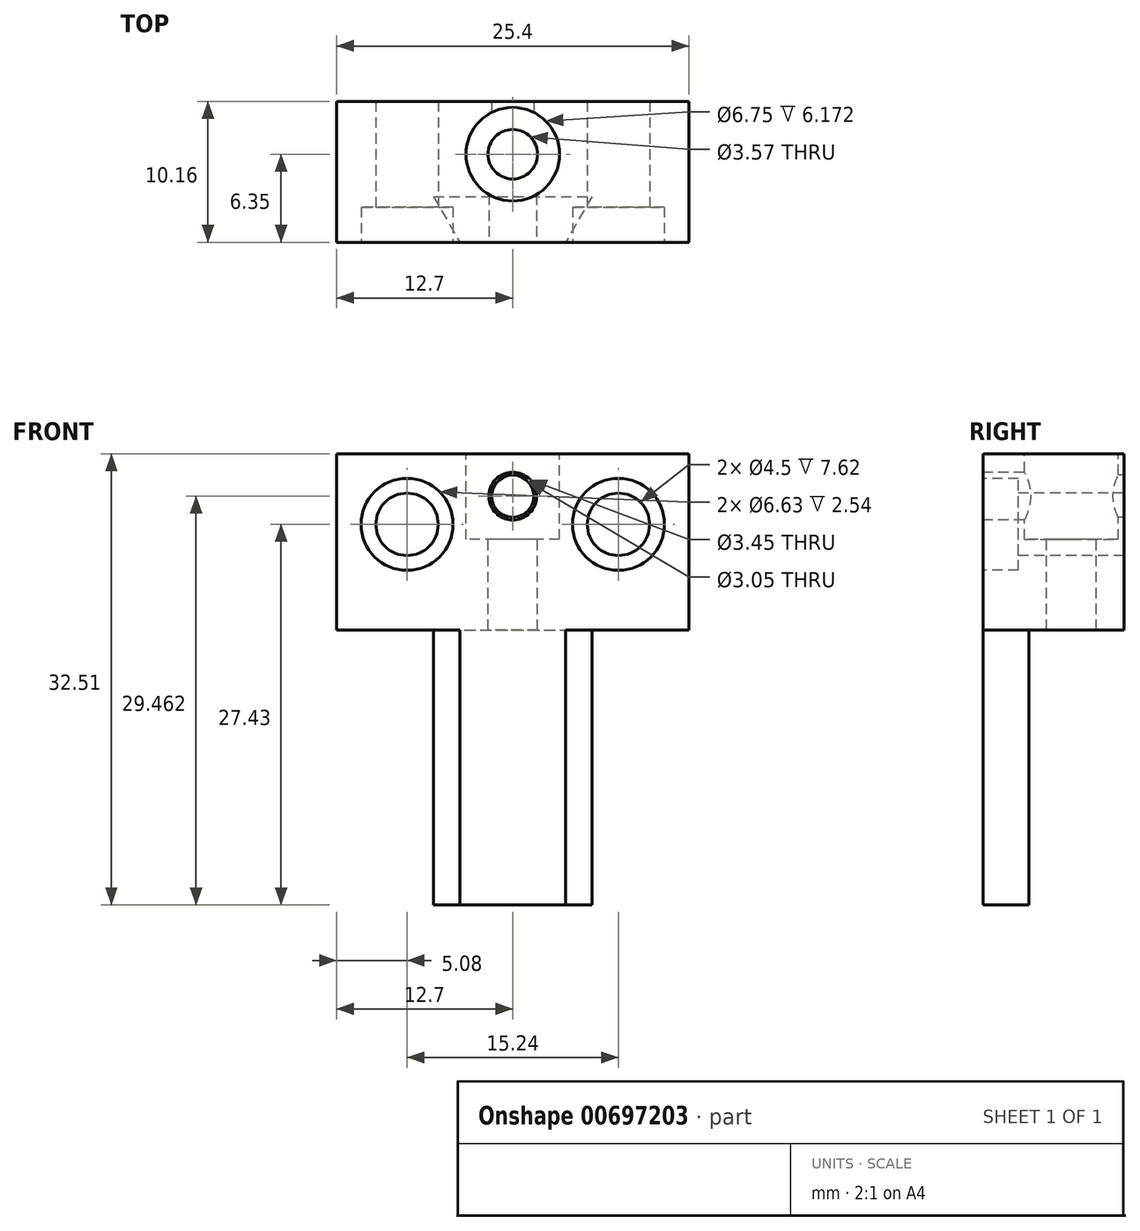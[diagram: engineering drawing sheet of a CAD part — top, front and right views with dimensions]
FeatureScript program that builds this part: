
annotation { "Feature Type Name" : "Feature", "Feature Type Description" : "" }
export const myFeature = defineFeature(function(context is Context, id is Id, definition is map)
    precondition{}
    {
        {
            var Q0;
            Q0=qCreatedBy(makeId("Top.planeOp"),FACE);
            var sketch = newSketch(context, id + "F0", { "sketchPlane" : qUnion([Q0])});
            skLineSegment(sketch, "E0.bottom", {"start": v(0, 0) * mm, "end": v(25.4, 0) * mm});
            skLineSegment(sketch, "E0.top", {"start": v(0, 10.16) * mm, "end": v(25.4, 10.16) * mm});
            skLineSegment(sketch, "E0.left", {"start": v(0, 0) * mm, "end": v(0, 10.16) * mm});
            skLineSegment(sketch, "E0.right", {"start": v(25.4, 0) * mm, "end": v(25.4, 10.16) * mm});
            skSolve(sketch);
        }
        {
            var Q0;
            Q0=makeQuery(id+"F0.imprint","IMPRINT",FACE,{"disambiguationData":[TD([[makeQuery(id+"F0.imprint","IMPRINT",EDGE,{"derivedFrom":sQuery(id+"F0.wireOp",EDGE,"E0.bottom")}),1.0]])]});
            extrude(context, id + "F1", {"entities" : qUnion([Q0]), "depth" : 12.7 * mm, "offsetDistance" : 25.4 * mm});
        }
        {
            var Q0;
            Q0=makeQuery(id+"F1.opExtrude","CAP_FACE",FACE,{"disambiguationData":[OSD([sQuery(id+"F0.wireOp",EDGE,"E0.bottom"),sQuery(id+"F0.wireOp",EDGE,"E0.top"),sQuery(id+"F0.wireOp",EDGE,"E0.left"),sQuery(id+"F0.wireOp",EDGE,"E0.right")])],"isStart":true});
            var sketch = newSketch(context, id + "F2", { "sketchPlane" : qUnion([Q0])});
            skLineSegment(sketch, "E1", {"start": v(0, -3.3) * mm, "end": v(6.99, -3.3) * mm});
            skLineSegment(sketch, "E2", {"start": v(6.99, -3.3) * mm, "end": v(8.9, 0) * mm});
            skLineSegment(sketch, "E3", {"start": v(6.99, -3.3) * mm, "end": v(18.41, -3.3) * mm});
            skLineSegment(sketch, "E4", {"start": v(18.41, -3.3) * mm, "end": v(16.5, 0) * mm});
            skLineSegment(sketch, "E5", {"start": v(8.9, 0) * mm, "end": v(16.5, 0) * mm});
            skSolve(sketch);
        }
        {
            var Q0;
            Q0=makeQuery(id+"F2.imprint","IMPRINT",FACE,{"disambiguationData":[TD([[makeQuery(id+"F2.imprint","IMPRINT",EDGE,{"derivedFrom":sQuery(id+"F2.wireOp",EDGE,"E2")}),-1.0]])]});
            extrude(context, id + "F3", {"entities" : qUnion([Q0]), "operationType" : NewBodyOperationType.ADD, "depth" : 19.8 * mm, "offsetDistance" : 25.4 * mm});
        }
        {
            var Q0;
            Q0=makeQuery(id+"F3.boolean.opBoolean","MERGE",FACE,{"derivedFrom":[makeQuery(id+"F1.opExtrude","SWEPT_FACE",FACE,{"disambiguationData":[OSD([sQuery(id+"F0.wireOp",EDGE,"E0.bottom")])]}),makeQuery(id+"F3.opExtrude","SWEPT_FACE",FACE,{"disambiguationData":[OSD([sQuery(id+"F2.wireOp",EDGE,"E5")])]})]});
            var sketch = newSketch(context, id + "F4", { "sketchPlane" : qUnion([Q0])});
            skLineSegment(sketch, "E6", {"start": v(0, 7.62) * mm, "end": v(5.08, 7.62) * mm});
            skLineSegment(sketch, "E7", {"start": v(5.08, 7.62) * mm, "end": v(5.08, 12.7) * mm});
            skLineSegment(sketch, "E8", {"start": v(5.08, 7.62) * mm, "end": v(20.32, 7.62) * mm});
            skLineSegment(sketch, "E9", {"start": v(20.32, 7.62) * mm, "end": v(20.32, 12.7) * mm});
            skLineSegment(sketch, "E10", {"start": v(20.32, 7.62) * mm, "end": v(25.4, 7.62) * mm});
            skLineSegment(sketch, "E11", {"start": v(12.7, 12.7) * mm, "end": v(12.7, 9.65) * mm});
            skLineSegment(sketch, "E12", {"start": v(12.7, 9.65) * mm, "end": v(0, 9.65) * mm});
            skSolve(sketch);
        }
        {
            var Q0;
            Q0=sQuery(id+"F4.wireOp",VERTEX,"E8.start");
            var Q1;
            Q1=sQuery(id+"F4.wireOp",VERTEX,"E10.start");
            var Q2;
            Q2=makeQuery(id+"F1.opExtrude","SWEPT_BODY",BODY,{"disambiguationData":[OSD([sQuery(id+"F0.wireOp",EDGE,"E0.bottom"),sQuery(id+"F0.wireOp",EDGE,"E0.top"),sQuery(id+"F0.wireOp",EDGE,"E0.left"),sQuery(id+"F0.wireOp",EDGE,"E0.right")])]});
            hole(context, id + "F5", {"style" : HoleStyle.C_BORE, "endStyle" : HoleEndStyle.THROUGH, "holeDiameter" : 4.5 * mm, "cBoreDiameter" : 6.63 * mm, "cBoreDepth" : 2.54 * mm, "majorDiameter" : 6.35 * mm, "isTappedThrough" : true, "tappedDepth" : 12.7 * mm, "tapClearance" : 3, "locations" : qUnion([Q0, Q1]), "scope" : qUnion([Q2])});
        }
        {
            var Q0;
            Q0=makeQuery(id+"F1.opExtrude","CAP_FACE",FACE,{"disambiguationData":[OSD([sQuery(id+"F0.wireOp",EDGE,"E0.bottom"),sQuery(id+"F0.wireOp",EDGE,"E0.top"),sQuery(id+"F0.wireOp",EDGE,"E0.left"),sQuery(id+"F0.wireOp",EDGE,"E0.right")])],"isStart":false});
            var sketch = newSketch(context, id + "F6", { "sketchPlane" : qUnion([Q0])});
            skLineSegment(sketch, "E13", {"start": v(12.7, 10.16) * mm, "end": v(12.7, 6.35) * mm});
            skLineSegment(sketch, "E14", {"start": v(12.7, 6.35) * mm, "end": v(25.4, 6.35) * mm});
            skSolve(sketch);
        }
        {
            var Q0;
            Q0=sQuery(id+"F6.wireOp",VERTEX,"E13.end");
            var Q1;
            Q1=makeQuery(id+"F1.opExtrude","SWEPT_BODY",BODY,{"disambiguationData":[OSD([sQuery(id+"F0.wireOp",EDGE,"E0.bottom"),sQuery(id+"F0.wireOp",EDGE,"E0.top"),sQuery(id+"F0.wireOp",EDGE,"E0.left"),sQuery(id+"F0.wireOp",EDGE,"E0.right")])]});
            hole(context, id + "F7", {"style" : HoleStyle.C_BORE, "endStyle" : HoleEndStyle.THROUGH, "holeDiameter" : 3.57 * mm, "cBoreDiameter" : 6.75 * mm, "cBoreDepth" : 6.17 * mm, "majorDiameter" : 6.35 * mm, "isTappedThrough" : true, "tappedDepth" : 12.7 * mm, "tapClearance" : 3, "locations" : qUnion([Q0]), "scope" : qUnion([Q1])});
        }
        {
            var Q0;
            Q0=sQuery(id+"F4.wireOp",VERTEX,"E12.start");
            var Q1;
            Q1=makeQuery(id+"F1.opExtrude","SWEPT_BODY",BODY,{"disambiguationData":[OSD([sQuery(id+"F0.wireOp",EDGE,"E0.bottom"),sQuery(id+"F0.wireOp",EDGE,"E0.top"),sQuery(id+"F0.wireOp",EDGE,"E0.left"),sQuery(id+"F0.wireOp",EDGE,"E0.right")])]});
            hole(context, id + "F8", {"style" : HoleStyle.SIMPLE, "endStyle" : HoleEndStyle.BLIND, "standardTappedOrClearance" : lookupTablePath({ "standard" : "ANSI", "engagement" : "75%", "pitch" : "32 tpi", "size" : "#8", "type" : "Tapped" }), "standardBlindInLast" : lookupTablePath({ "standard" : "ANSI", "engagement" : "75%", "pitch" : "32 tpi", "size" : "#8", "type" : "Tapped" }), "holeDiameter" : 3.45 * mm, "majorDiameter" : 4.17 * mm, "showTappedDepth" : true, "holeDepth" : 6.35 * mm, "isTappedThrough" : true, "tappedDepth" : 3.97 * mm, "tapClearance" : 3, "locations" : qUnion([Q0]), "scope" : qUnion([Q1])});
        }
        {
            var Q0;
            Q0=sQuery(id+"F4.wireOp",VERTEX,"E12.start");
            var Q1;
            Q1=makeQuery(id+"F1.opExtrude","SWEPT_BODY",BODY,{"disambiguationData":[OSD([sQuery(id+"F0.wireOp",EDGE,"E0.bottom"),sQuery(id+"F0.wireOp",EDGE,"E0.top"),sQuery(id+"F0.wireOp",EDGE,"E0.left"),sQuery(id+"F0.wireOp",EDGE,"E0.right")])]});
            hole(context, id + "F9", {"style" : HoleStyle.SIMPLE, "endStyle" : HoleEndStyle.THROUGH, "holeDiameter" : 3.05 * mm, "majorDiameter" : 6.35 * mm, "isTappedThrough" : true, "tappedDepth" : 12.7 * mm, "tapClearance" : 3, "locations" : qUnion([Q0]), "scope" : qUnion([Q1])});
        }
    });
